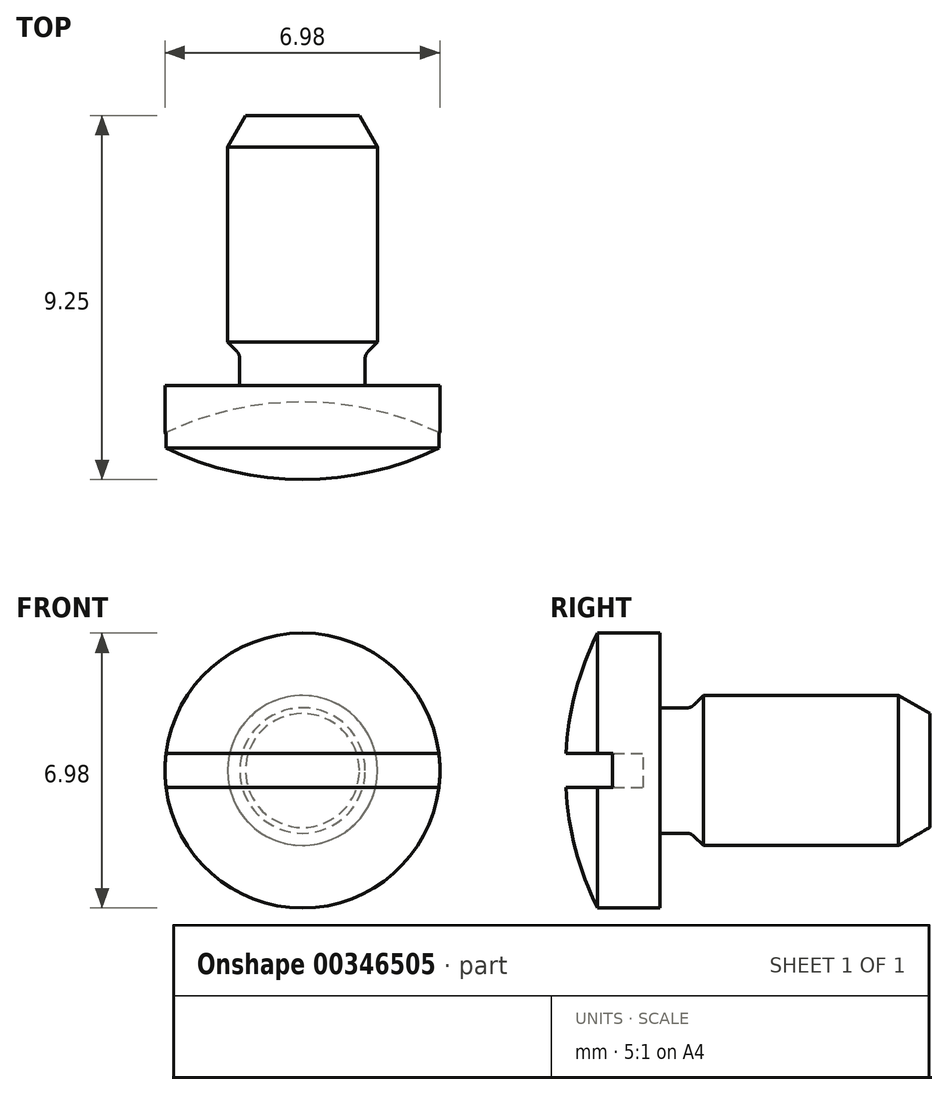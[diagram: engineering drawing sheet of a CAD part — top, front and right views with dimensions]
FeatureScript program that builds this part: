
annotation { "Feature Type Name" : "Feature", "Feature Type Description" : "" }
export const myFeature = defineFeature(function(context is Context, id is Id, definition is map)
    precondition{}
    {
        {
            var Q0;
            Q0=qCreatedBy(makeId("Right.planeOp"),FACE);
            var sketch = newSketch(context, id + "F0", { "sketchPlane" : qUnion([Q0])});
            skLineSegment(sketch, "E0.bottom", {"start": v(0, 0) * mm, "end": v(1.59, 0) * mm});
            skLineSegment(sketch, "E0.top", {"start": v(0, 3.5) * mm, "end": v(1.59, 3.5) * mm});
            skLineSegment(sketch, "E0.left", {"start": v(0, 0) * mm, "end": v(0, 3.5) * mm, "construction": true});
            skLineSegment(sketch, "E0.right", {"start": v(1.59, 0) * mm, "end": v(1.59, 3.5) * mm});
            skLineSegment(sketch, "E1", {"start": v(18.35, 0) * mm, "end": v(0, 0) * mm, "construction": true});
            skArc(sketch, "E2", {"start": v(0, 3.5) * mm, "mid": v(-0.6, 1.8) * mm, "end": v(-0.8, 0) * mm});
            skLineSegment(sketch, "E3", {"start": v(0, 0) * mm, "end": v(-0.8, 0) * mm});
            skSolve(sketch);
        }
        {
            var Q0;
            Q0 = qSketchRegion(id + "F0", true);
            var Q1;
            Q1=sQuery(id+"F0.wireOp",EDGE,"E1");
            revolve(context, id + "F1", {"entities" : qUnion([Q0]), "axis" : qUnion([Q1]), "revolveType" : RevolveType.FULL});
        }
        {
            var Q0;
            Q0=qCreatedBy(makeId("Right.planeOp"),FACE);
            var sketch = newSketch(context, id + "F2", { "sketchPlane" : qUnion([Q0])});
            skLineSegment(sketch, "E4", {"start": v(1.59, 1.6) * mm, "end": v(2.38, 1.6) * mm});
            skLineSegment(sketch, "E5.0", {"start": v(1.59, 1.6) * mm, "end": v(1.59, 0) * mm});
            skLineSegment(sketch, "E6", {"start": v(2.38, 1.6) * mm, "end": v(2.38, 1.9) * mm, "construction": true});
            skLineSegment(sketch, "E7", {"start": v(0, 0) * mm, "end": v(17.86, 0) * mm, "construction": true});
            skPoint(sketch, "E8.orphan", {"position": v(1.59, 3.5) * mm});
            skPoint(sketch, "E9.orphan", {"position": v(1.59, -3.5) * mm});
            skLineSegment(sketch, "E10", {"start": v(2.7, 1.9) * mm, "end": v(7.65, 1.9) * mm});
            skLineSegment(sketch, "E11", {"start": v(8.45, 1.45) * mm, "end": v(8.45, 0) * mm});
            skLineSegment(sketch, "E12", {"start": v(1.59, 0) * mm, "end": v(8.45, 0) * mm});
            skLineSegment(sketch, "E13", {"start": v(2.38, 1.6) * mm, "end": v(2.7, 1.9) * mm});
            skLineSegment(sketch, "E14", {"start": v(8.45, 1.45) * mm, "end": v(7.65, 1.9) * mm});
            skSolve(sketch);
        }
        {
            var Q0;
            Q0=makeQuery(id+"F2.imprint","IMPRINT",FACE,{"disambiguationData":[TD([[makeQuery(id+"F2.imprint","IMPRINT",EDGE,{"derivedFrom":sQuery(id+"F2.wireOp",EDGE,"E4")}),-1.0]])]});
            var Q1;
            Q1=sQuery(id+"F2.wireOp",EDGE,"E7");
            revolve(context, id + "F3", {"operationType" : NewBodyOperationType.ADD, "entities" : qUnion([Q0]), "axis" : qUnion([Q1]), "revolveType" : RevolveType.FULL});
        }
        {
            var Q0;
            Q0=makeQuery(id+"F3.opRevolve","SWEPT_EDGE",EDGE,{"disambiguationData":[OSD([sQuery(id+"F2.wireOp",EDGE,"E4"),sQuery(id+"F2.wireOp",EDGE,"E5.0")])]});
            var Q1;
            Q1=makeQuery(id+"F3.opRevolve","SWEPT_EDGE",EDGE,{"disambiguationData":[OSD([sQuery(id+"F2.wireOp",EDGE,"E4"),sQuery(id+"F2.wireOp",EDGE,"E13")])]});
            fillet(context, id + "F4", {"entities" : qUnion([Q0, Q1]), "radius" : 0.25 * mm, "tangentPropagation" : true, "allowEdgeOverflow" : false});
        }
        {
            var Q0;
            Q0=qCreatedBy(makeId("Top.planeOp"),FACE);
            var sketch = newSketch(context, id + "F5", { "sketchPlane" : qUnion([Q0])});
            skLineSegment(sketch, "E15.0", {"start": v(0, 0) * mm, "end": v(0, -0.8) * mm, "construction": true});
            skLineSegment(sketch, "E16", {"start": v(-3.5, 0.38) * mm, "end": v(3.5, 0.38) * mm, "construction": true});
            skLineSegment(sketch, "E17", {"start": v(0, 0) * mm, "end": v(0, 0.38) * mm, "construction": true});
            skLineSegment(sketch, "E18", {"start": v(0, -0.8) * mm, "end": v(0, -6.9) * mm, "construction": true});
            skArc(sketch, "E19", {"start": v(3.5, 0.38) * mm, "mid": v(0, 1.17) * mm, "end": v(-3.5, 0.38) * mm});
            skLineSegment(sketch, "E20", {"start": v(0, 0.38) * mm, "end": v(0, 1.17) * mm, "construction": true});
            skPoint(sketch, "E20.endSnap0", {"position": v(0, 1.17) * mm});
            skPoint(sketch, "E21.orphan", {"position": v(0, 1.32) * mm});
            skLineSegment(sketch, "E22", {"start": v(-3.5, 0.38) * mm, "end": v(-3.5, -1.4) * mm});
            skLineSegment(sketch, "E23", {"start": v(-3.5, -1.4) * mm, "end": v(3.5, -1.4) * mm});
            skLineSegment(sketch, "E24", {"start": v(3.5, -1.4) * mm, "end": v(3.5, 0.38) * mm});
            skSolve(sketch);
        }
        {
            var Q0;
            Q0 = qSketchRegion(id + "F5", true);
            extrude(context, id + "F6", {"entities" : qUnion([Q0]), "operationType" : NewBodyOperationType.REMOVE, "flatOperationType" : FlatOperationType.REMOVE, "oppositeDirection" : true, "offsetDistance" : 25.4 * mm, "depth" : 0.86 * mm, "domain" : OperationDomain.MODEL, "symmetric" : true});
        }
    });
